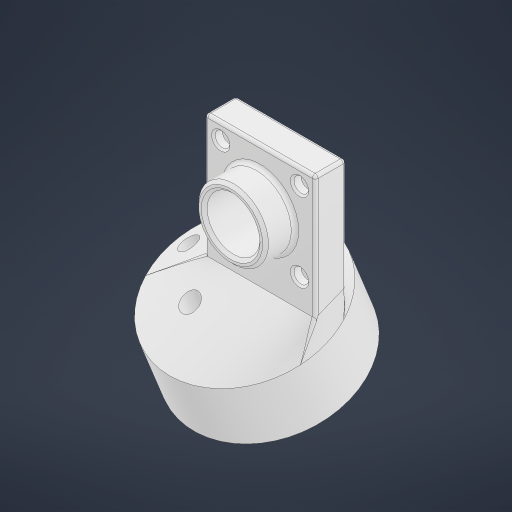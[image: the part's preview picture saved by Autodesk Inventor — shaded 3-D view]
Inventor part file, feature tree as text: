
AUTODESK INVENTOR PART (.ipt)
format: ipt  version: 2023.4 (Build 274418000, 418)  size: 533,504 bytes
history: native  units: in
note: dims shown in document units (in); Inventor stores cm internally (conversion verified against a paired STEP export)
features: extrude x8, hole x3, fillet x3, other x3, projected_geometry x3, plane x2, chamfer x2, sketch x2, loft x1, thicken_offset x1, revolve x1
ambient origin geometry x8: Origin, YZ Plane, XZ Plane, XY Plane, X Axis, Y Axis, Z Axis, Center Point
bodies: Solid1 (feature_tree)
feature tree (29):
  extrude  "Extrusion1"  Depth=0.525in
  extrude  "Extrusion2"  Depth=0.4673in
  plane  "Work Plane1"
  extrude  "Extrusion3"  Depth=1.875in TaperAngle=0.0deg
  loft  "Loft1"
  extrude  "Extrusion4"  Depth=2.75in
  hole  "Hole1"  [1 undecoded]
  extrude  "Extrusion5"  TaperAngle=0.0deg  [1 undecoded]
  extrude  "Extrusion6"  TaperAngle=0.0deg  [1 undecoded]
  hole  "Hole2"  [1 undecoded]
  plane  "Work Plane2"
  fillet  "Fillet1"  Radius=0.3in
  chamfer  "Chamfer1"  Distance=1.1875in
  fillet  "Fillet2"  Radius=0.5in
  extrude  "Extrusion7"  Depth=0.1839in
  fillet  "Fillet3"  Radius=1.3386in
  chamfer  "Chamfer2"  Distance=0.15in
  thicken_offset  "Thicken1"
  hole  "Hole4"  [1 undecoded]
  extrude  "Extrusion8"  Depth=0.9792in
  other  "Edges1"
  other  "Edges2"
  projected_geometry  "Projected Loop1"
  projected_geometry  "Projected Loop2"
  sketch  "Sketch11"  dims[d0=1.875in d1=0.525in]
  other  "Srf1"
  sketch  "Sketch12"  dims[d2=1.875in d3=0.0in d4=0.4673in d5=1.875in d6=0.0in d7=0.6in d9=2.75in d10=0.1in d11=0.0in d12=0.0in d13=90.0deg d14=0.0in d15=90.0deg d16=1.6in d17=0.3in d18=0.0in d19=0.9in d20=0.75in d21=0.119in d22=0.25in d23=0.6871in d24=1.0in d25=0.8108in d26=1.1875in d27=0.5in d28=0.0in d29=0.1839in d30=1.3386in d31=0.15in d32=0.0in d33=0.094in d34=0.75in d35=0.251in d36=0.15in d37=0.6871in d38=1.0in d39=0.8108in d40=0.9792in d41=0.9792in d42=315.0deg d52=0.05in d53=0.05in d54=0.125in d55=45.0deg d56=0.0625in d57=1.0in d58=1.0in d59=0.0in d60=0.25in d61=0.0312in d62=0.125in d63=45.0deg d64=0.2405in d65=90.0deg d66=1.0in d67=1.0in d68=0.177in d69=0.75in d70=0.313in d71=1.45in d72=0.5635in d73=1.0in d74=0.8108in d75=1.25in d76=0.87in d77=1.0in d78=0.0in]
  revolve  "RevolutionSrf1"  Angle=315.0deg
  projected_geometry  "Project Cut Edges1"
note: 5 required parameter values undecoded (feature->parameter linkage not recoverable at this tier; creation-order binding heuristic only, values carry confidence <= 0.55)
